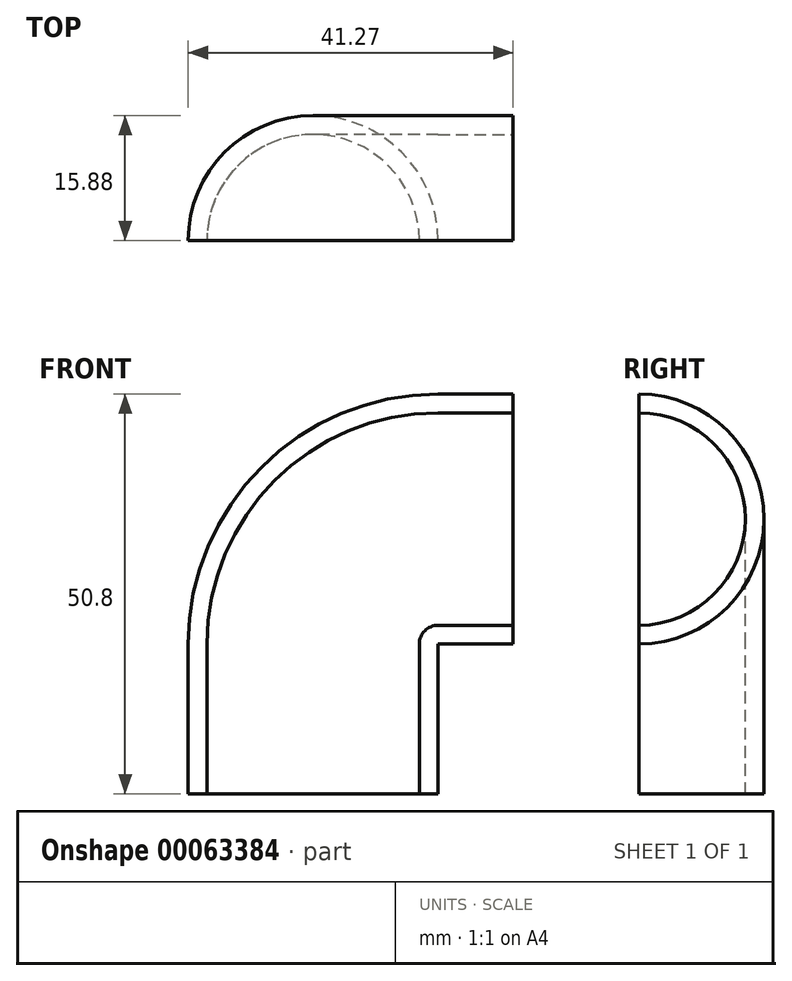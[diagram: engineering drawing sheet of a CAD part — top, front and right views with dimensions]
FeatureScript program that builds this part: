
annotation { "Feature Type Name" : "Feature", "Feature Type Description" : "" }
export const myFeature = defineFeature(function(context is Context, id is Id, definition is map)
    precondition{}
    {
        {
            var Q0;
            Q0=qCreatedBy(makeId("Front.planeOp"),FACE);
            var sketch = newSketch(context, id + "F0", { "sketchPlane" : qUnion([Q0])});
            skLineSegment(sketch, "E0", {"start": v(0, 0) * mm, "end": v(0, 19.05) * mm});
            skLineSegment(sketch, "E1", {"start": v(31.75, 50.8) * mm, "end": v(50.8, 50.8) * mm});
            skPoint(sketch, "E2.visualSharp", {"position": v(0, 50.8) * mm});
            skArc(sketch, "E2.filletArc", {"start": v(31.75, 50.8) * mm, "mid": v(9.3, 41.5) * mm, "end": v(0, 19.05) * mm});
            skSolve(sketch);
        }
        {
            var Q0;
            Q0=qCreatedBy(makeId("Top.planeOp"),FACE);
            var sketch = newSketch(context, id + "F1", { "sketchPlane" : qUnion([Q0])});
            skArc(sketch, "E3", {"start": v(31.75, 0) * mm, "mid": v(15.88, 15.88) * mm, "end": v(0, 0) * mm});
            skArc(sketch, "E4", {"start": v(29.37, 0) * mm, "mid": v(15.88, 13.5) * mm, "end": v(2.38, 0) * mm});
            skLineSegment(sketch, "E5", {"start": v(42.37, 0) * mm, "end": v(-17.83, 0) * mm, "construction": true});
            skLineSegment(sketch, "E6", {"start": v(31.75, 0) * mm, "end": v(29.37, 0) * mm});
            skLineSegment(sketch, "E7", {"start": v(2.38, 0) * mm, "end": v(0, 0) * mm});
            skSolve(sketch);
        }
        {
            var Q0;
            Q0=makeQuery(id+"F1.imprint","IMPRINT",FACE,{"disambiguationData":[TD([[makeQuery(id+"F1.imprint","IMPRINT",EDGE,{"derivedFrom":sQuery(id+"F1.wireOp",EDGE,"E3")}),1.0]])]});
            var Q1;
            Q1=sQuery(id+"F0.wireOp",EDGE,"E0");
            var Q2;
            Q2=sQuery(id+"F0.wireOp",EDGE,"E2.filletArc");
            var Q3;
            Q3=sQuery(id+"F0.wireOp",EDGE,"E1");
            sweep(context, id + "F2", {"profiles" : qUnion([Q0]), "path" : qUnion([Q1, Q2, Q3])});
        }
        {
            var Q0;
            Q0=makeQuery(id+"F2.opSweep","CAP_FACE",FACE,{"disambiguationData":[OSD([sQuery(id+"F0.wireOp",VERTEX,"E1.end"),sQuery(id+"F1.wireOp",EDGE,"E3"),sQuery(id+"F1.wireOp",EDGE,"E4")])],"isStart":false});
            var sketch = newSketch(context, id + "F3", { "sketchPlane" : qUnion([Q0])});
            skCircle(sketch, "E8", {"center": v(0, 34.93) * mm, "radius": 15.95 * mm});
            skSolve(sketch);
        }
        {
            var Q0;
            Q0=qSketchRegion(id+"F3",true);
            extrude(context, id + "F4", {"entities" : qUnion([Q0]), "operationType" : NewBodyOperationType.REMOVE, "oppositeDirection" : true, "depth" : 9.52 * mm});
        }
    });
